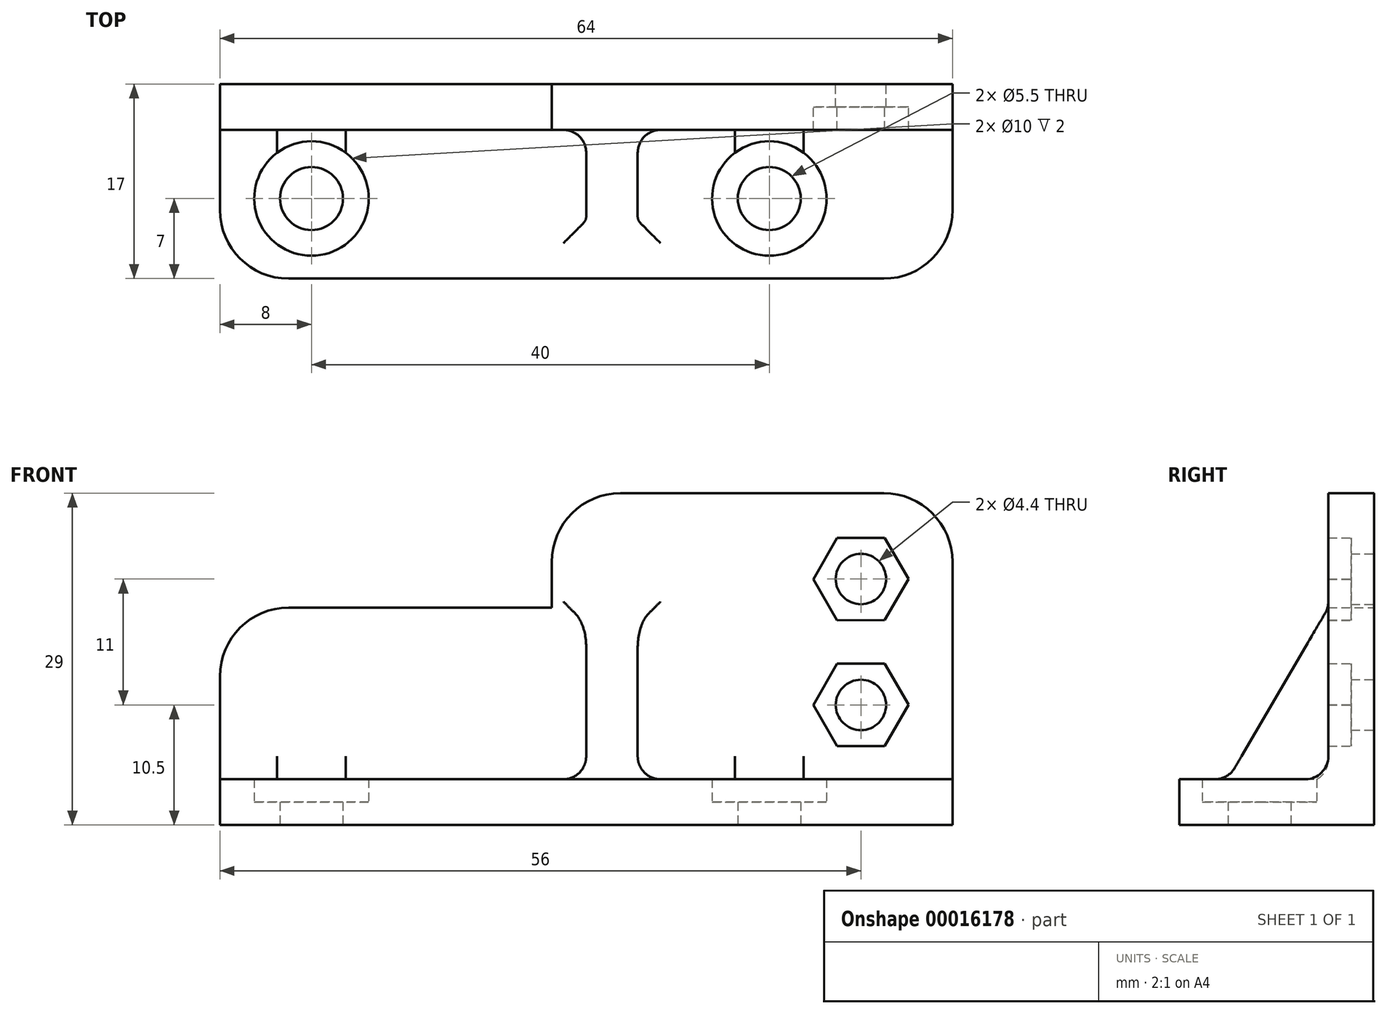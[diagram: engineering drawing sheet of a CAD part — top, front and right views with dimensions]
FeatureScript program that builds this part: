
annotation { "Feature Type Name" : "Feature", "Feature Type Description" : "" }
export const myFeature = defineFeature(function(context is Context, id is Id, definition is map)
    precondition{}
    {
        {
            var Q0;
            Q0=qCreatedBy(makeId("Top.planeOp"),FACE);
            var sketch = newSketch(context, id + "F0", { "sketchPlane" : qUnion([Q0])});
            skCircle(sketch, "E0", {"center": v(16, -10) * mm, "radius": 5 * mm});
            skLineSegment(sketch, "E1.bottom", {"start": v(-32, 0) * mm, "end": v(32, 0) * mm});
            skLineSegment(sketch, "E1.top", {"start": v(-26, -17) * mm, "end": v(26, -17) * mm});
            skLineSegment(sketch, "E1.left", {"start": v(-32, 0) * mm, "end": v(-32, -11) * mm});
            skLineSegment(sketch, "E1.right", {"start": v(32, 0) * mm, "end": v(32, -11) * mm});
            skCircle(sketch, "E2", {"center": v(16, -10) * mm, "radius": 2.75 * mm});
            skLineSegment(sketch, "E3", {"start": v(16, -10) * mm, "end": v(-24, -10) * mm, "construction": true});
            skCircle(sketch, "E4", {"center": v(-24, -10) * mm, "radius": 2.75 * mm});
            skCircle(sketch, "E5", {"center": v(-24, -10) * mm, "radius": 5 * mm});
            skPoint(sketch, "E6.visualSharp", {"position": v(-32, -17) * mm});
            skArc(sketch, "E6.filletArc", {"start": v(-32, -11) * mm, "mid": v(-30.24, -15.24) * mm, "end": v(-26, -17) * mm});
            skPoint(sketch, "E7.visualSharp", {"position": v(32, -17) * mm});
            skArc(sketch, "E7.filletArc", {"start": v(26, -17) * mm, "mid": v(30.24, -15.24) * mm, "end": v(32, -11) * mm});
            skSolve(sketch);
        }
        {
            var Q0;
            Q0=makeQuery(id+"F0.imprint","IMPRINT",FACE,{"disambiguationData":[TD([[makeQuery(id+"F0.imprint","IMPRINT",EDGE,{"derivedFrom":sQuery(id+"F0.wireOp",EDGE,"E0")}),-1.0]])]});
            var Q1;
            Q1=makeQuery(id+"F0.imprint","IMPRINT",FACE,{"disambiguationData":[TD([[makeQuery(id+"F0.imprint","IMPRINT",EDGE,{"derivedFrom":sQuery(id+"F0.wireOp",EDGE,"E4")}),-1.0]])]});
            var Q2;
            Q2=makeQuery(id+"F0.imprint","IMPRINT",FACE,{"disambiguationData":[TD([[makeQuery(id+"F0.imprint","IMPRINT",EDGE,{"derivedFrom":sQuery(id+"F0.wireOp",EDGE,"E0")}),1.0]])]});
            extrude(context, id + "F1", {"entities" : qUnion([Q0, Q1, Q2]), "depth" : 4 * mm});
        }
        {
            var Q0;
            Q0=makeQuery(id+"F0.imprint","IMPRINT",FACE,{"disambiguationData":[TD([[makeQuery(id+"F0.imprint","IMPRINT",EDGE,{"derivedFrom":sQuery(id+"F0.wireOp",EDGE,"E4")}),-1.0]])]});
            var Q1;
            Q1=makeQuery(id+"F0.imprint","IMPRINT",FACE,{"disambiguationData":[TD([[makeQuery(id+"F0.imprint","IMPRINT",EDGE,{"derivedFrom":sQuery(id+"F0.wireOp",EDGE,"E0")}),1.0]])]});
            extrude(context, id + "F2", {"entities" : qUnion([Q0, Q1]), "operationType" : NewBodyOperationType.REMOVE, "depth" : 4 * mm, "hasSecondDirection" : true, "secondDirectionOppositeDirection" : false, "secondDirectionDepth" : 2 * mm});
        }
        {
            var Q0;
            Q0=qCreatedBy(makeId("Front.planeOp"),FACE);
            var sketch = newSketch(context, id + "F3", { "sketchPlane" : qUnion([Q0])});
            skLineSegment(sketch, "E8.bottom", {"start": v(-32, 0) * mm, "end": v(32, 0) * mm});
            skLineSegment(sketch, "E8.top", {"start": v(-26, 19) * mm, "end": v(-3, 19) * mm});
            skLineSegment(sketch, "E8.left", {"start": v(-32, 0) * mm, "end": v(-32, 13) * mm});
            skLineSegment(sketch, "E8.right", {"start": v(32, 0) * mm, "end": v(32, 19) * mm});
            skCircle(sketch, "E9", {"center": v(24, 10.5) * mm, "radius": 2.2 * mm});
            skCircle(sketch, "E10", {"center": v(24, 21.5) * mm, "radius": 2.2 * mm});
            skLineSegment(sketch, "E11.top", {"start": v(26, 29) * mm, "end": v(3, 29) * mm});
            skLineSegment(sketch, "E11.left", {"start": v(32, 19) * mm, "end": v(32, 23) * mm});
            skLineSegment(sketch, "E11.right", {"start": v(-3, 19) * mm, "end": v(-3, 23) * mm});
            skPoint(sketch, "E12.visualSharp", {"position": v(32, 29) * mm});
            skArc(sketch, "E12.filletArc", {"start": v(32, 23) * mm, "mid": v(30.24, 27.24) * mm, "end": v(26, 29) * mm});
            skPoint(sketch, "E13.visualSharp", {"position": v(-3, 29) * mm});
            skArc(sketch, "E13.filletArc", {"start": v(3, 29) * mm, "mid": v(-1.24, 27.24) * mm, "end": v(-3, 23) * mm});
            skPoint(sketch, "E14.visualSharp", {"position": v(-32, 19) * mm});
            skArc(sketch, "E14.filletArc", {"start": v(-26, 19) * mm, "mid": v(-30.24, 17.24) * mm, "end": v(-32, 13) * mm});
            skSolve(sketch);
        }
        {
            var Q0;
            Q0=makeQuery(id+"F3.imprint","IMPRINT",FACE,{"disambiguationData":[TD([[makeQuery(id+"F3.imprint","IMPRINT",EDGE,{"derivedFrom":sQuery(id+"F3.wireOp",EDGE,"E8.bottom")}),1.0]])]});
            extrude(context, id + "F4", {"entities" : qUnion([Q0]), "operationType" : NewBodyOperationType.ADD, "depth" : 4 * mm});
        }
        {
            var Q0;
            Q0=qCreatedBy(makeId("Front.planeOp"),FACE);
            var sketch = newSketch(context, id + "F5", { "sketchPlane" : qUnion([Q0])});
            skCircle(sketch, "E15.cCircle", {"center": v(24, 10.5) * mm, "radius": 3.6 * mm, "construction": true});
            skLineSegment(sketch, "E15.0", {"start": v(28.16, 10.51) * mm, "end": v(26.09, 6.9) * mm});
            skLineSegment(sketch, "E15.1", {"start": v(26.09, 6.9) * mm, "end": v(21.93, 6.9) * mm});
            skLineSegment(sketch, "E15.2", {"start": v(21.93, 6.9) * mm, "end": v(19.84, 10.49) * mm});
            skLineSegment(sketch, "E15.3", {"start": v(19.84, 10.49) * mm, "end": v(21.91, 14.1) * mm});
            skLineSegment(sketch, "E15.4", {"start": v(21.91, 14.1) * mm, "end": v(26.07, 14.1) * mm});
            skLineSegment(sketch, "E15.5", {"start": v(26.07, 14.1) * mm, "end": v(28.16, 10.51) * mm});
            skPoint(sketch, "E15.0.midPoint", {"position": v(27.12, 8.7) * mm});
            skLineSegment(sketch, "E16.4", {"start": v(21.91, 25.1) * mm, "end": v(26.07, 25.1) * mm});
            skCircle(sketch, "E16.cCircle", {"center": v(24, 21.5) * mm, "radius": 3.6 * mm, "construction": true});
            skLineSegment(sketch, "E16.5", {"start": v(26.07, 25.1) * mm, "end": v(28.16, 21.51) * mm});
            skLineSegment(sketch, "E16.0", {"start": v(28.16, 21.51) * mm, "end": v(26.09, 17.9) * mm});
            skLineSegment(sketch, "E16.1", {"start": v(26.09, 17.9) * mm, "end": v(21.93, 17.9) * mm});
            skLineSegment(sketch, "E16.2", {"start": v(21.93, 17.9) * mm, "end": v(19.84, 21.49) * mm});
            skLineSegment(sketch, "E16.3", {"start": v(19.84, 21.49) * mm, "end": v(21.91, 25.1) * mm});
            skSolve(sketch);
        }
        {
            var Q0;
            Q0=qCreatedBy(makeId("Right.planeOp"),FACE);
            var sketch = newSketch(context, id + "F6", { "sketchPlane" : qUnion([Q0])});
            skLineSegment(sketch, "E17", {"start": v(0, 0) * mm, "end": v(-15.1, 0) * mm});
            skLineSegment(sketch, "E18", {"start": v(-15.1, 0) * mm, "end": v(0, 25.83) * mm});
            skLineSegment(sketch, "E19", {"start": v(0, 25.83) * mm, "end": v(0, 0) * mm});
            skSolve(sketch);
        }
        {
            var Q0;
            Q0=makeQuery(id+"F5.imprint","IMPRINT",FACE,{"disambiguationData":[TD([[makeQuery(id+"F5.imprint","IMPRINT",EDGE,{"derivedFrom":sQuery(id+"F5.wireOp",EDGE,"E15.0")}),-1.0]])]});
            var Q1;
            Q1=makeQuery(id+"F5.imprint","IMPRINT",FACE,{"disambiguationData":[TD([[makeQuery(id+"F5.imprint","IMPRINT",EDGE,{"derivedFrom":sQuery(id+"F5.wireOp",EDGE,"E16.4")}),-1.0]])]});
            extrude(context, id + "F7", {"entities" : qUnion([Q0, Q1]), "operationType" : NewBodyOperationType.REMOVE, "depth" : 4 * mm, "hasSecondDirection" : true, "secondDirectionOppositeDirection" : false, "secondDirectionDepth" : 2 * mm});
        }
        {
            var Q0;
            Q0=makeQuery(id+"F6.imprint","IMPRINT",FACE,{"disambiguationData":[TD([[makeQuery(id+"F6.imprint","IMPRINT",EDGE,{"derivedFrom":sQuery(id+"F6.wireOp",EDGE,"E17")}),-1.0]])]});
            extrude(context, id + "F8", {"entities" : qUnion([Q0]), "operationType" : NewBodyOperationType.ADD, "depth" : 4.5 * mm});
        }
        {
            var Q0;
            {var subQ0=sQuery(id+"F0.wireOp",EDGE,"E1.right");var subQ1=makeQuery(id+"F1.opExtrude","CAP_FACE",FACE,{"disambiguationData":[OSD([sQuery(id+"F0.wireOp",EDGE,"E1.bottom"),sQuery(id+"F0.wireOp",EDGE,"E1.top"),sQuery(id+"F0.wireOp",EDGE,"E1.left"),subQ0,sQuery(id+"F0.wireOp",EDGE,"E2"),sQuery(id+"F0.wireOp",EDGE,"E4"),sQuery(id+"F0.wireOp",EDGE,"E6.filletArc"),sQuery(id+"F0.wireOp",EDGE,"E7.filletArc")])],"isStart":false});var subQ2=sQuery(id+"F3.wireOp",EDGE,"E8.right");var subQ3=sQuery(id+"F3.wireOp",EDGE,"E11.left");var subQ4=makeQuery(id+"F4.opExtrude","CAP_FACE",FACE,{"disambiguationData":[OSD([sQuery(id+"F3.wireOp",EDGE,"E8.bottom"),sQuery(id+"F3.wireOp",EDGE,"E8.top"),sQuery(id+"F3.wireOp",EDGE,"E8.left"),subQ2,sQuery(id+"F3.wireOp",EDGE,"E9"),sQuery(id+"F3.wireOp",EDGE,"E10"),sQuery(id+"F3.wireOp",EDGE,"E11.top"),subQ3,sQuery(id+"F3.wireOp",EDGE,"E11.right"),sQuery(id+"F3.wireOp",EDGE,"E12.filletArc"),sQuery(id+"F3.wireOp",EDGE,"E13.filletArc"),sQuery(id+"F3.wireOp",EDGE,"E14.filletArc")])],"isStart":false});Q0=makeQuery(id+"F8.boolean.opBoolean","SPLIT",EDGE,{"disambiguationData":[TD([makeQuery(id+"F1.opExtrude","SWEPT_FACE",FACE,{"disambiguationData":[OSD([subQ0])]})])],"derivedFrom":makeQuery(id+"F4.boolean.opBoolean","INTERSECT",EDGE,{"derivedFrom":[subQ1,subQ4]})});}
            var Q1;
            {var subQ0=sQuery(id+"F0.wireOp",EDGE,"E1.left");var subQ1=makeQuery(id+"F1.opExtrude","CAP_FACE",FACE,{"disambiguationData":[OSD([sQuery(id+"F0.wireOp",EDGE,"E1.bottom"),sQuery(id+"F0.wireOp",EDGE,"E1.top"),subQ0,sQuery(id+"F0.wireOp",EDGE,"E1.right"),sQuery(id+"F0.wireOp",EDGE,"E2"),sQuery(id+"F0.wireOp",EDGE,"E4"),sQuery(id+"F0.wireOp",EDGE,"E6.filletArc"),sQuery(id+"F0.wireOp",EDGE,"E7.filletArc")])],"isStart":false});var subQ2=sQuery(id+"F3.wireOp",EDGE,"E8.left");var subQ3=makeQuery(id+"F4.opExtrude","CAP_FACE",FACE,{"disambiguationData":[OSD([sQuery(id+"F3.wireOp",EDGE,"E8.bottom"),sQuery(id+"F3.wireOp",EDGE,"E8.top"),subQ2,sQuery(id+"F3.wireOp",EDGE,"E8.right"),sQuery(id+"F3.wireOp",EDGE,"E9"),sQuery(id+"F3.wireOp",EDGE,"E10"),sQuery(id+"F3.wireOp",EDGE,"E11.top"),sQuery(id+"F3.wireOp",EDGE,"E11.left"),sQuery(id+"F3.wireOp",EDGE,"E11.right"),sQuery(id+"F3.wireOp",EDGE,"E12.filletArc"),sQuery(id+"F3.wireOp",EDGE,"E13.filletArc"),sQuery(id+"F3.wireOp",EDGE,"E14.filletArc")])],"isStart":false});Q1=makeQuery(id+"F8.boolean.opBoolean","SPLIT",EDGE,{"disambiguationData":[TD([makeQuery(id+"F1.opExtrude","SWEPT_FACE",FACE,{"disambiguationData":[OSD([subQ0])]})])],"derivedFrom":makeQuery(id+"F4.boolean.opBoolean","INTERSECT",EDGE,{"derivedFrom":[subQ1,subQ3]})});}
            var Q2;
            Q2=makeQuery(id+"F8.boolean.opBoolean","INTERSECT",EDGE,{"derivedFrom":[makeQuery(id+"F1.opExtrude","CAP_FACE",FACE,{"disambiguationData":[OSD([sQuery(id+"F0.wireOp",EDGE,"E1.bottom"),sQuery(id+"F0.wireOp",EDGE,"E1.top"),sQuery(id+"F0.wireOp",EDGE,"E1.left"),sQuery(id+"F0.wireOp",EDGE,"E1.right"),sQuery(id+"F0.wireOp",EDGE,"E2"),sQuery(id+"F0.wireOp",EDGE,"E4"),sQuery(id+"F0.wireOp",EDGE,"E6.filletArc"),sQuery(id+"F0.wireOp",EDGE,"E7.filletArc")])],"isStart":false}),makeQuery(id+"F8.opExtrude","CAP_FACE",FACE,{"disambiguationData":[OSD([sQuery(id+"F6.wireOp",EDGE,"E17"),sQuery(id+"F6.wireOp",EDGE,"E18"),sQuery(id+"F6.wireOp",EDGE,"E19")])],"isStart":false})]});
            var Q3;
            Q3=makeQuery(id+"F8.boolean.opBoolean","INTERSECT",EDGE,{"derivedFrom":[makeQuery(id+"F1.opExtrude","CAP_FACE",FACE,{"disambiguationData":[OSD([sQuery(id+"F0.wireOp",EDGE,"E1.bottom"),sQuery(id+"F0.wireOp",EDGE,"E1.top"),sQuery(id+"F0.wireOp",EDGE,"E1.left"),sQuery(id+"F0.wireOp",EDGE,"E1.right"),sQuery(id+"F0.wireOp",EDGE,"E2"),sQuery(id+"F0.wireOp",EDGE,"E4"),sQuery(id+"F0.wireOp",EDGE,"E6.filletArc"),sQuery(id+"F0.wireOp",EDGE,"E7.filletArc")])],"isStart":false}),makeQuery(id+"F8.opExtrude","SWEPT_FACE",FACE,{"disambiguationData":[OSD([sQuery(id+"F6.wireOp",EDGE,"E18")])]})]});
            var Q4;
            Q4=makeQuery(id+"F8.boolean.opBoolean","INTERSECT",EDGE,{"derivedFrom":[makeQuery(id+"F1.opExtrude","CAP_FACE",FACE,{"disambiguationData":[OSD([sQuery(id+"F0.wireOp",EDGE,"E1.bottom"),sQuery(id+"F0.wireOp",EDGE,"E1.top"),sQuery(id+"F0.wireOp",EDGE,"E1.left"),sQuery(id+"F0.wireOp",EDGE,"E1.right"),sQuery(id+"F0.wireOp",EDGE,"E2"),sQuery(id+"F0.wireOp",EDGE,"E4"),sQuery(id+"F0.wireOp",EDGE,"E6.filletArc"),sQuery(id+"F0.wireOp",EDGE,"E7.filletArc")])],"isStart":false}),makeQuery(id+"F8.opExtrude","CAP_FACE",FACE,{"disambiguationData":[OSD([sQuery(id+"F6.wireOp",EDGE,"E17"),sQuery(id+"F6.wireOp",EDGE,"E18"),sQuery(id+"F6.wireOp",EDGE,"E19")])],"isStart":true})]});
            var Q5;
            Q5=makeQuery(id+"F8.boolean.opBoolean","INTERSECT",EDGE,{"derivedFrom":[makeQuery(id+"F4.opExtrude","CAP_FACE",FACE,{"disambiguationData":[OSD([sQuery(id+"F3.wireOp",EDGE,"E8.bottom"),sQuery(id+"F3.wireOp",EDGE,"E8.top"),sQuery(id+"F3.wireOp",EDGE,"E8.left"),sQuery(id+"F3.wireOp",EDGE,"E8.right"),sQuery(id+"F3.wireOp",EDGE,"E9"),sQuery(id+"F3.wireOp",EDGE,"E10"),sQuery(id+"F3.wireOp",EDGE,"E11.top"),sQuery(id+"F3.wireOp",EDGE,"E11.left"),sQuery(id+"F3.wireOp",EDGE,"E11.right"),sQuery(id+"F3.wireOp",EDGE,"E12.filletArc"),sQuery(id+"F3.wireOp",EDGE,"E13.filletArc"),sQuery(id+"F3.wireOp",EDGE,"E14.filletArc")])],"isStart":false}),makeQuery(id+"F8.opExtrude","CAP_FACE",FACE,{"disambiguationData":[OSD([sQuery(id+"F6.wireOp",EDGE,"E17"),sQuery(id+"F6.wireOp",EDGE,"E18"),sQuery(id+"F6.wireOp",EDGE,"E19")])],"isStart":true})]});
            var Q6;
            Q6=makeQuery(id+"F8.boolean.opBoolean","INTERSECT",EDGE,{"derivedFrom":[makeQuery(id+"F4.opExtrude","CAP_FACE",FACE,{"disambiguationData":[OSD([sQuery(id+"F3.wireOp",EDGE,"E8.bottom"),sQuery(id+"F3.wireOp",EDGE,"E8.top"),sQuery(id+"F3.wireOp",EDGE,"E8.left"),sQuery(id+"F3.wireOp",EDGE,"E8.right"),sQuery(id+"F3.wireOp",EDGE,"E9"),sQuery(id+"F3.wireOp",EDGE,"E10"),sQuery(id+"F3.wireOp",EDGE,"E11.top"),sQuery(id+"F3.wireOp",EDGE,"E11.left"),sQuery(id+"F3.wireOp",EDGE,"E11.right"),sQuery(id+"F3.wireOp",EDGE,"E12.filletArc"),sQuery(id+"F3.wireOp",EDGE,"E13.filletArc"),sQuery(id+"F3.wireOp",EDGE,"E14.filletArc")])],"isStart":false}),makeQuery(id+"F8.opExtrude","SWEPT_FACE",FACE,{"disambiguationData":[OSD([sQuery(id+"F6.wireOp",EDGE,"E18")])]})]});
            var Q7;
            Q7=makeQuery(id+"F8.boolean.opBoolean","INTERSECT",EDGE,{"derivedFrom":[makeQuery(id+"F4.opExtrude","CAP_FACE",FACE,{"disambiguationData":[OSD([sQuery(id+"F3.wireOp",EDGE,"E8.bottom"),sQuery(id+"F3.wireOp",EDGE,"E8.top"),sQuery(id+"F3.wireOp",EDGE,"E8.left"),sQuery(id+"F3.wireOp",EDGE,"E8.right"),sQuery(id+"F3.wireOp",EDGE,"E9"),sQuery(id+"F3.wireOp",EDGE,"E10"),sQuery(id+"F3.wireOp",EDGE,"E11.top"),sQuery(id+"F3.wireOp",EDGE,"E11.left"),sQuery(id+"F3.wireOp",EDGE,"E11.right"),sQuery(id+"F3.wireOp",EDGE,"E12.filletArc"),sQuery(id+"F3.wireOp",EDGE,"E13.filletArc"),sQuery(id+"F3.wireOp",EDGE,"E14.filletArc")])],"isStart":false}),makeQuery(id+"F8.opExtrude","CAP_FACE",FACE,{"disambiguationData":[OSD([sQuery(id+"F6.wireOp",EDGE,"E17"),sQuery(id+"F6.wireOp",EDGE,"E18"),sQuery(id+"F6.wireOp",EDGE,"E19")])],"isStart":false})]});
            fillet(context, id + "F9", {"entities" : qUnion([Q0, Q1, Q2, Q3, Q4, Q5, Q6, Q7]), "radius" : 2 * mm, "tangentPropagation" : true, "allowEdgeOverflow" : false});
        }
    });
